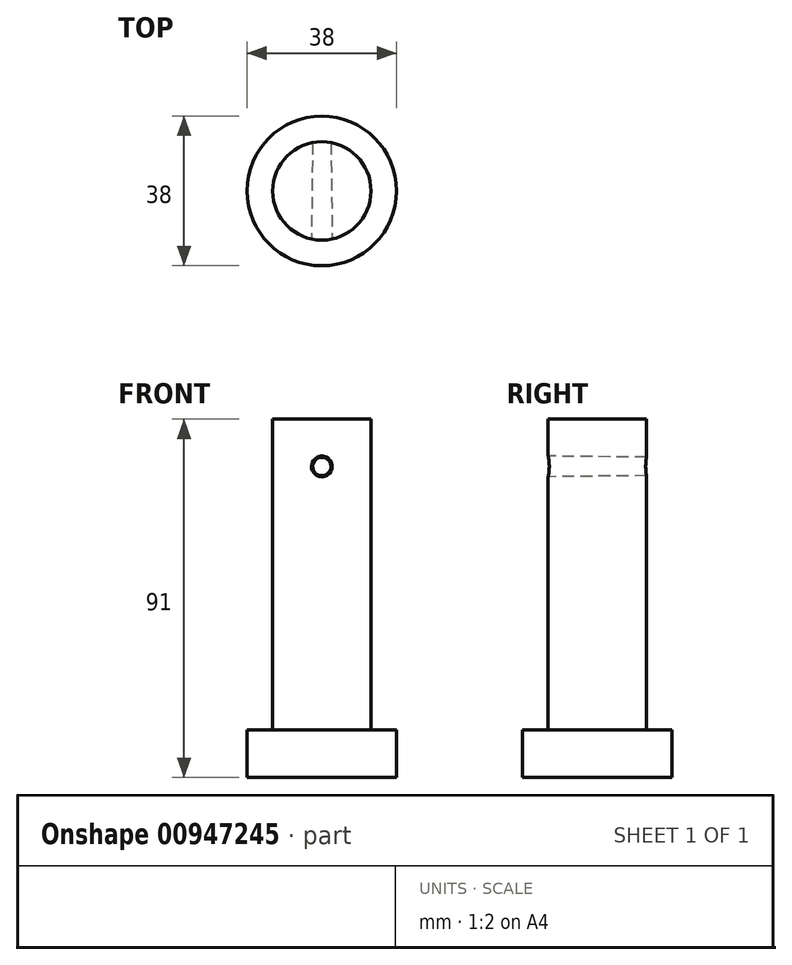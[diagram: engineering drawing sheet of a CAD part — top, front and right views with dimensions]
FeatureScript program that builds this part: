
annotation { "Feature Type Name" : "Feature", "Feature Type Description" : "" }
export const myFeature = defineFeature(function(context is Context, id is Id, definition is map)
    precondition{}
    {
        {
            var Q0;
            Q0=qCreatedBy(makeId("Right.planeOp"),FACE);
            var sketch = newSketch(context, id + "F0", { "sketchPlane" : qUnion([Q0])});
            skLineSegment(sketch, "E0", {"start": v(0, 45.5) * mm, "end": v(0, -45.5) * mm, "construction": true});
            skLineSegment(sketch, "E1", {"start": v(0, 45.5) * mm, "end": v(12.5, 45.5) * mm});
            skLineSegment(sketch, "E2", {"start": v(12.5, 45.5) * mm, "end": v(12.5, 39.5) * mm});
            skLineSegment(sketch, "E3", {"start": v(12.5, 39.5) * mm, "end": v(12.5, 39.5) * mm});
            skLineSegment(sketch, "E4", {"start": v(12.5, 39.5) * mm, "end": v(12.5, 27.5) * mm});
            skLineSegment(sketch, "E5", {"start": v(12.5, 27.5) * mm, "end": v(12.5, 27.5) * mm});
            skLineSegment(sketch, "E6", {"start": v(12.5, 27.5) * mm, "end": v(12.5, -33.5) * mm});
            skLineSegment(sketch, "E7", {"start": v(12.5, -33.5) * mm, "end": v(19, -33.5) * mm});
            skLineSegment(sketch, "E8", {"start": v(19, -33.5) * mm, "end": v(19, -45.5) * mm});
            skLineSegment(sketch, "E9", {"start": v(19, -45.5) * mm, "end": v(0, -45.5) * mm});
            skLineSegment(sketch, "E10", {"start": v(0, 45.5) * mm, "end": v(0, -45.5) * mm});
            skLineSegment(sketch, "E11", {"start": v(0, 82.42) * mm, "end": v(0, -86.26) * mm, "construction": true});
            skSolve(sketch);
        }
        {
            var Q0;
            Q0=makeQuery(id+"F0.imprint","IMPRINT",FACE,{"disambiguationData":[TD([[makeQuery(id+"F0.imprint","IMPRINT",EDGE,{"derivedFrom":sQuery(id+"F0.wireOp",EDGE,"E1")}),-1.0]])]});
            var Q1;
            Q1=sQuery(id+"F0.wireOp",EDGE,"E11");
            revolve(context, id + "F1", {"surfaceOperationType" : NewSurfaceOperationType.NEW, "entities" : qUnion([Q0]), "axis" : qUnion([Q1]), "revolveType" : RevolveType.FULL});
        }
        {
            var Q0;
            Q0=qCreatedBy(makeId("Front.planeOp"),FACE);
            cPlane(context, id + "F2", {"entities" : qUnion([Q0]), "cplaneType" : CPlaneType.OFFSET, "offset" : 29 * mm, "width" : 150 * mm, "height" : 150 * mm});
        }
        {
            var Q0;
            Q0=qCreatedBy(id+"F2.planeOp",FACE);
            var sketch = newSketch(context, id + "F3", { "sketchPlane" : qUnion([Q0])});
            skCircle(sketch, "E12", {"center": v(0, 33.5) * mm, "radius": 2.81 * mm});
            skSolve(sketch);
        }
        {
            var Q0;
            Q0=qCreatedBy(makeId("Front.planeOp"),FACE);
            cPlane(context, id + "F4", {"entities" : qUnion([Q0]), "cplaneType" : CPlaneType.OFFSET, "offset" : 29 * mm, "oppositeDirection" : true, "width" : 150 * mm, "height" : 150 * mm});
        }
        {
            var Q0;
            Q0=qCreatedBy(id+"F4.planeOp",FACE);
            var sketch = newSketch(context, id + "F5", { "sketchPlane" : qUnion([Q0])});
            skCircle(sketch, "E13", {"center": v(0, 64.25) * mm, "radius": 2.15 * mm});
            skCircle(sketch, "E14", {"center": v(0, 33.5) * mm, "radius": 2.16 * mm});
            skSolve(sketch);
        }
        {
            var Q1;
            Q1=makeQuery(id+"F3.imprint","IMPRINT",FACE,{"disambiguationData":[TD([[makeQuery(id+"F3.imprint","IMPRINT",EDGE,{"derivedFrom":sQuery(id+"F3.wireOp",EDGE,"E12")}),1.0]])]});
            var Q2;
            Q2=makeQuery(id+"F5.imprint","IMPRINT",FACE,{"disambiguationData":[TD([[makeQuery(id+"F5.imprint","IMPRINT",EDGE,{"derivedFrom":sQuery(id+"F5.wireOp",EDGE,"E14")}),1.0]])]});
            loft(context, id + "F6", {"operationType" : NewBodyOperationType.REMOVE, "sheetProfilesArray" : [{ "sheetProfileEntities" : qUnion([Q1]) }, { "sheetProfileEntities" : qUnion([Q2]) }]});
        }
    });
